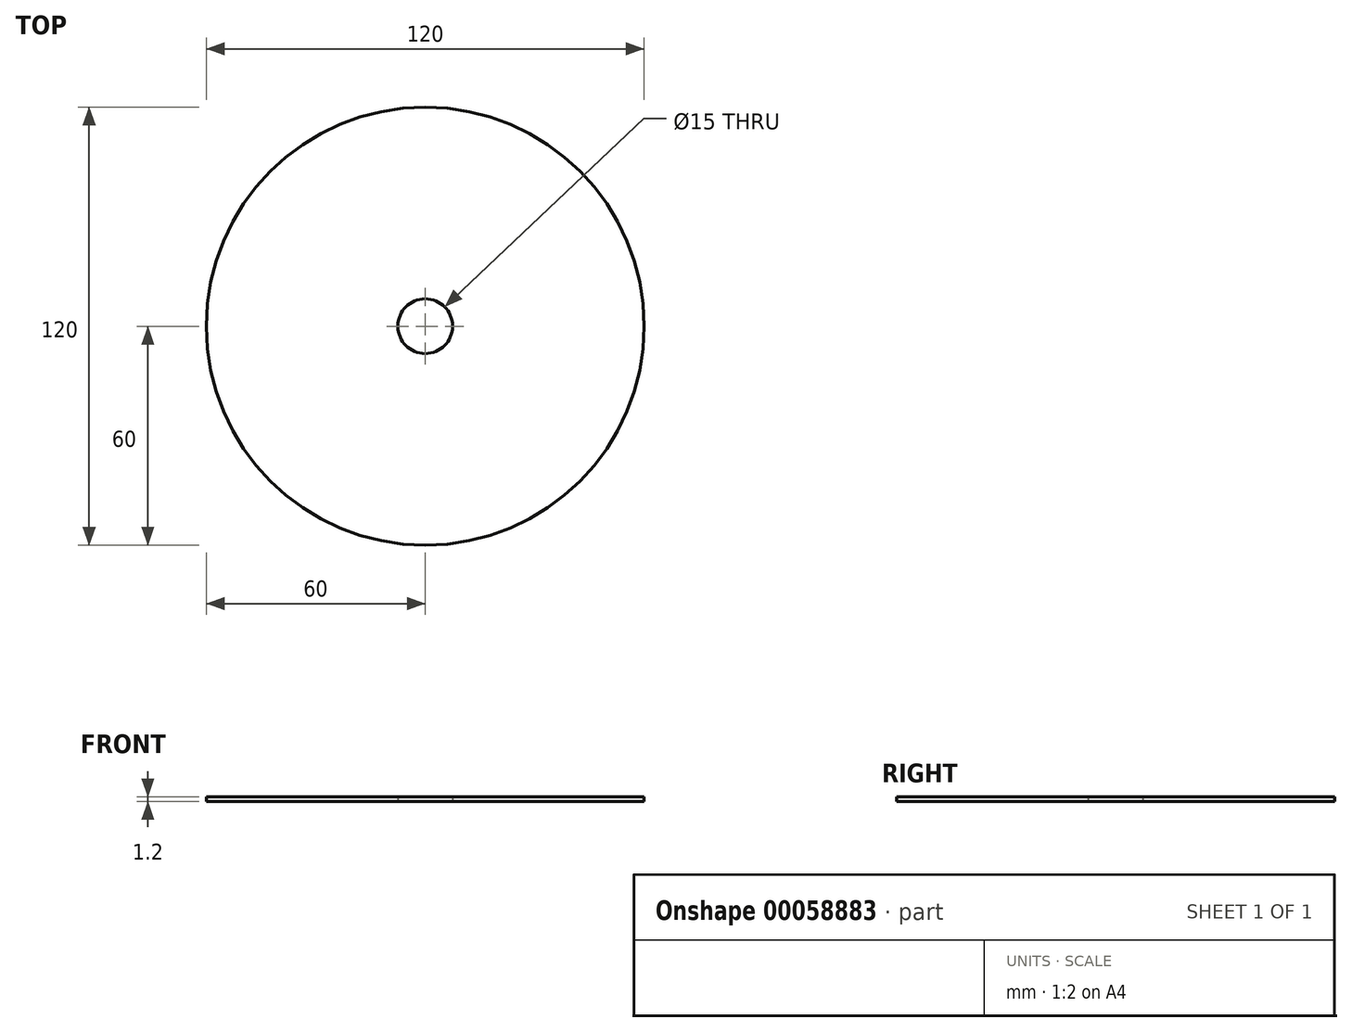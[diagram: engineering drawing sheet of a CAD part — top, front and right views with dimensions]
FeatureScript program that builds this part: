
annotation { "Feature Type Name" : "Feature", "Feature Type Description" : "" }
export const myFeature = defineFeature(function(context is Context, id is Id, definition is map)
    precondition{}
    {
        {
            var Q0;
            Q0=qCreatedBy(makeId("Top.planeOp"),FACE);
            var sketch = newSketch(context, id + "F0", { "sketchPlane" : qUnion([Q0])});
            skCircle(sketch, "E0", {"center": v(0, 0) * mm, "radius": 60 * mm});
            skCircle(sketch, "E1", {"center": v(0, 0) * mm, "radius": 7.5 * mm});
            skSolve(sketch);
        }
        {
            var Q0;
            Q0 = qSketchRegion(id + "F0", true);
            extrude(context, id + "F1", {"entities" : qUnion([Q0]), "depth" : 1.2 * mm});
        }
    });
